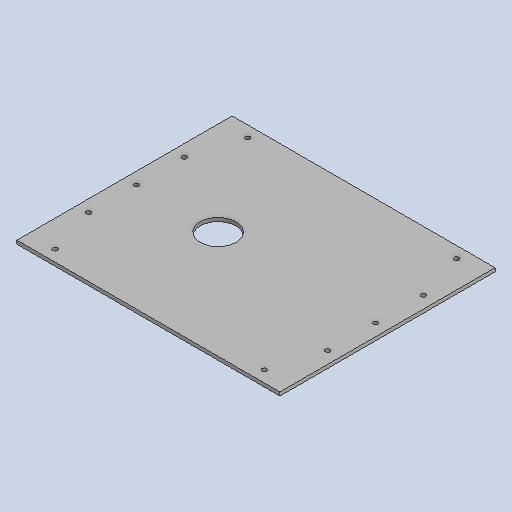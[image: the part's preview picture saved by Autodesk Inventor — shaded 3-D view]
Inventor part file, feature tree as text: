
AUTODESK INVENTOR PART (.ipt)
format: ipt  version: 2022 (Build 260153000, 153)  size: 116,736 bytes
history: native  units: mm
features: other x9, reference x5, extrude x4, sketch x4
ambient origin geometry x8: Origin, YZ Plane, XZ Plane, XY Plane, X Axis, Y Axis, Z Axis, Center Point
bodies: Body1 (feature_tree)
feature tree (22):
  other  "Твердое тело1"
  extrude  "Выдавливание3"  Depth=220.0mm TaperAngle=0.0deg
  extrude  "Выдавливание4"  Depth=3.0mm TaperAngle=0.0deg
  sketch  "Эскиз3"
  reference  "Ссылка1"
  reference  "Ссылка2"
  reference  "Ссылка3"
  reference  "Ссылка4"
  sketch  "Эскиз4"
  reference  "Ссылка5"
  sketch  "Эскиз1"
  sketch  "Эскиз2"
  other  "<path> - Robot.iam"
  other  "000.000 - Robot.iam"
  other  "01_Крепление_мотора:3"
  other  "01_Крепление_мотора:4"
  other  "01_Крепление_мотора:2"
  other  "01_Крепление_мотора:1"
  other  "000.100 - Electronic box:1"
  other  "000.101 - Bottom:1"
  extrude  "Выдавливание1"  Depth=10.0mm TaperAngle=0.0deg
  extrude  "Выдавливание2"  Depth=10.0mm TaperAngle=0.0deg
note: 1 file-system path scrubbed to <path> (originals preserved in map.json)
